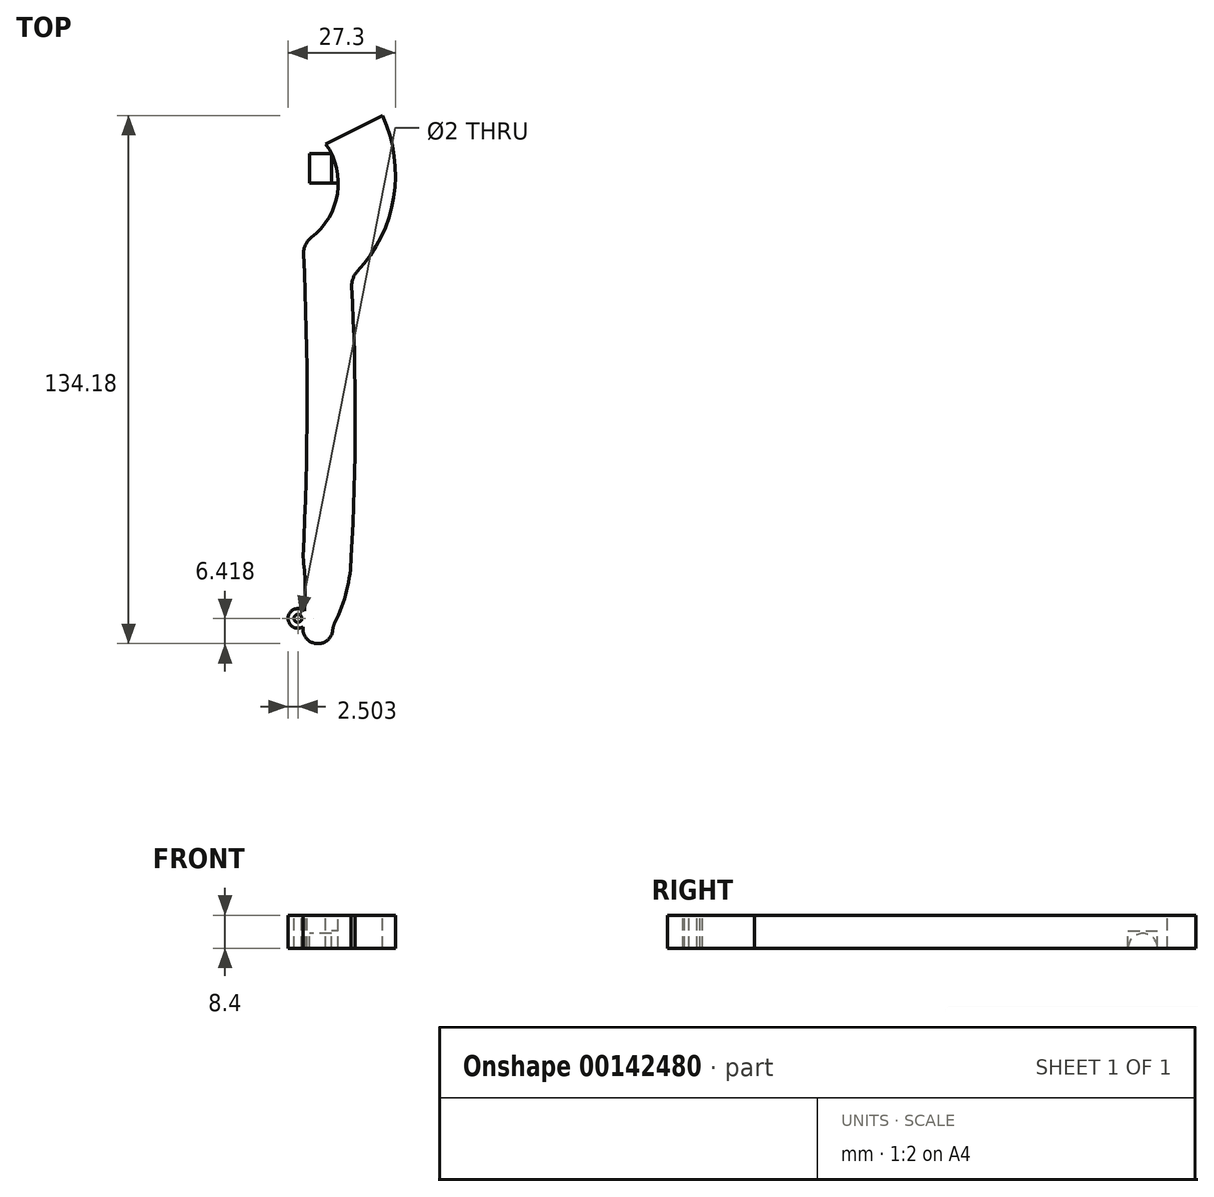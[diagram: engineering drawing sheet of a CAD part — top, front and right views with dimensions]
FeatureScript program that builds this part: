
annotation { "Feature Type Name" : "Feature", "Feature Type Description" : "" }
export const myFeature = defineFeature(function(context is Context, id is Id, definition is map)
    precondition{}
    {
        {
            var Q0;
            Q0=qCreatedBy(makeId("Top.planeOp"),FACE);
            var sketch = newSketch(context, id + "F0", { "sketchPlane" : qUnion([Q0])});
            skArc(sketch, "E0", {"start": v(-18.84, -33.1) * mm, "mid": v(-9.92, -17.2) * mm, "end": v(-18.84, -1.3) * mm});
            skArc(sketch, "E1", {"start": v(-9.22, -40.6) * mm, "mid": v(1.28, -22.3) * mm, "end": v(-0.84, -1.3) * mm});
            skArc(sketch, "E2", {"start": v(-18.84, -111.7) * mm, "mid": v(-17.84, -72.4) * mm, "end": v(-18.84, -33.1) * mm});
            skArc(sketch, "E3", {"start": v(-9.22, -112.4) * mm, "mid": v(-8.2, -76.5) * mm, "end": v(-9.22, -40.6) * mm});
            skArc(sketch, "E4", {"start": v(-18.84, -111.7) * mm, "mid": v(-14.2, -114.48) * mm, "end": v(-9.22, -112.4) * mm});
            skLineSegment(sketch, "E5", {"start": v(-0.84, -1.3) * mm, "end": v(-18.84, -1.3) * mm});
            skArc(sketch, "E6.0", {"start": v(-20.16, -112.1) * mm, "mid": v(-19.14, -72.24) * mm, "end": v(-20.18, -32.37) * mm});
            skLineSegment(sketch, "E6.1", {"start": v(0, 0) * mm, "end": v(-26.43, 0) * mm});
            skArc(sketch, "E6.2", {"start": v(-7.89, -41.14) * mm, "mid": v(2.7, -21.84) * mm, "end": v(0, 0) * mm});
            skArc(sketch, "E6.3", {"start": v(-20.18, -32.37) * mm, "mid": v(-11.53, -13.92) * mm, "end": v(-26.43, 0) * mm});
            skArc(sketch, "E6.4", {"start": v(-7.9, -112.1) * mm, "mid": v(-6.9, -76.62) * mm, "end": v(-7.89, -41.14) * mm});
            skArc(sketch, "E7", {"start": v(-20.16, -129.9) * mm, "mid": v(-19.6, -121) * mm, "end": v(-20.16, -112.1) * mm});
            skArc(sketch, "E8", {"start": v(-12.62, -129.9) * mm, "mid": v(-9.22, -121.28) * mm, "end": v(-7.9, -112.1) * mm});
            skArc(sketch, "E9", {"start": v(-20.16, -129.9) * mm, "mid": v(-16.4, -134.18) * mm, "end": v(-12.62, -129.9) * mm});
            skArc(sketch, "E10", {"start": v(-19.77, -125.92) * mm, "mid": v(-23.95, -127.51) * mm, "end": v(-20.16, -129.9) * mm});
            skCircle(sketch, "E11", {"center": v(-21.46, -127.76) * mm, "radius": 1 * mm});
            skLineSegment(sketch, "E12", {"start": v(-11.22, -17.2) * mm, "end": v(-18.52, -17.2) * mm});
            skLineSegment(sketch, "E13", {"start": v(-18.52, -17.2) * mm, "end": v(-18.52, -9.7) * mm});
            skLineSegment(sketch, "E14", {"start": v(-18.52, -9.7) * mm, "end": v(-12.93, -9.7) * mm});
            skLineSegment(sketch, "E15", {"start": v(0, 0) * mm, "end": v(-14.4, -7.2) * mm});
            skSolve(sketch);
        }
        {
            var Q0;
            {var subQ1=sQuery(id+"F0.wireOp",EDGE,"E1");Q0=makeQuery(id+"F0.imprint","IMPRINT",FACE,{"disambiguationData":[TD([[makeQuery(id+"F0.imprint","IMPRINT",EDGE,{"derivedFrom":subQ1}),1.0]])]});}
            var Q1;
            {var subQ8=sQuery(id+"F0.wireOp",EDGE,"E1");Q1=makeQuery(id+"F0.imprint","IMPRINT",FACE,{"disambiguationData":[TD([[makeQuery(id+"F0.imprint","IMPRINT",EDGE,{"derivedFrom":subQ8}),-1.0]])]});}
            var Q2;
            {var subQ0=sQuery(id+"F0.wireOp",EDGE,"E10");Q2=makeQuery(id+"F0.imprint","IMPRINT",FACE,{"disambiguationData":[TD([[makeQuery(id+"F0.imprint","IMPRINT",EDGE,{"derivedFrom":subQ0}),1.0]])]});}
            extrude(context, id + "F1", {"entities" : qUnion([Q0, Q1, Q2]), "oppositeDirection" : true, "depth" : 8.4 * mm});
        }
        {
            var Q0;
            {var subQ0=sQuery(id+"F0.wireOp",EDGE,"E12");Q0=makeQuery(id+"F0.imprint","IMPRINT",FACE,{"disambiguationData":[TD([[makeQuery(id+"F0.imprint","IMPRINT",EDGE,{"derivedFrom":subQ0}),-1.0]])]});}
            extrude(context, id + "F2", {"entities" : qUnion([Q0]), "operationType" : NewBodyOperationType.ADD, "oppositeDirection" : true, "depth" : 8.4 * mm});
        }
        {
            var Q0;
            {var subQ0=sQuery(id+"F0.wireOp",EDGE,"E12");Q0=makeQuery(id+"F0.imprint","IMPRINT",FACE,{"disambiguationData":[TD([[makeQuery(id+"F0.imprint","IMPRINT",EDGE,{"derivedFrom":subQ0}),-1.0]])]});}
            extrude(context, id + "F3", {"entities" : qUnion([Q0]), "operationType" : NewBodyOperationType.REMOVE, "oppositeDirection" : true, "depth" : 4 * mm});
        }
        {
            var Q0;
            Q0=makeQuery(id+"F2.opExtrude","SWEPT_FACE",FACE,{"disambiguationData":[OSD([sQuery(id+"F0.wireOp",EDGE,"E13")])]});
            var sketch = newSketch(context, id + "F4", { "sketchPlane" : qUnion([Q0])});
            skLineSegment(sketch, "E16.0", {"start": v(17.2, -8.4) * mm, "end": v(9.7, -8.4) * mm});
            skLineSegment(sketch, "E16.1", {"start": v(17.2, -8.4) * mm, "end": v(17.2, -4) * mm});
            skLineSegment(sketch, "E16.2", {"start": v(17.2, -4) * mm, "end": v(9.7, -4) * mm});
            skLineSegment(sketch, "E16.3", {"start": v(9.7, -8.4) * mm, "end": v(9.7, -4) * mm});
            skArc(sketch, "E17", {"start": v(17.2, -8.4) * mm, "mid": v(13.45, -4.65) * mm, "end": v(9.7, -8.4) * mm});
            skSolve(sketch);
        }
        {
            var Q0;
            Q0=makeQuery(id+"F4.imprint","IMPRINT",FACE,{"disambiguationData":[TD([[makeQuery(id+"F4.imprint","IMPRINT",EDGE,{"derivedFrom":sQuery(id+"F4.wireOp",EDGE,"E16.1")}),1.0]])]});
            extrude(context, id + "F5", {"entities" : qUnion([Q0]), "operationType" : NewBodyOperationType.REMOVE, "oppositeDirection" : true, "depth" : 5.6 * mm});
        }
        {
            var Q0;
            Q0=makeQuery(id+"F1.opExtrude","SWEPT_EDGE",EDGE,{"disambiguationData":[OSD([sQuery(id+"F0.wireOp",EDGE,"E6.2"),sQuery(id+"F0.wireOp",EDGE,"E6.4")])]});
            var Q1;
            Q1=makeQuery(id+"F1.opExtrude","SWEPT_EDGE",EDGE,{"disambiguationData":[OSD([sQuery(id+"F0.wireOp",EDGE,"E6.0"),sQuery(id+"F0.wireOp",EDGE,"E6.3")])]});
            var Q2;
            Q2=makeQuery(id+"F1.opExtrude","SWEPT_EDGE",EDGE,{"disambiguationData":[OSD([sQuery(id+"F0.wireOp",EDGE,"E8"),sQuery(id+"F0.wireOp",EDGE,"E9")])]});
            fillet(context, id + "F6", {"entities" : qUnion([Q0, Q1, Q2]), "radius" : 5 * mm, "tangentPropagation" : true, "allowEdgeOverflow" : false});
        }
    });
